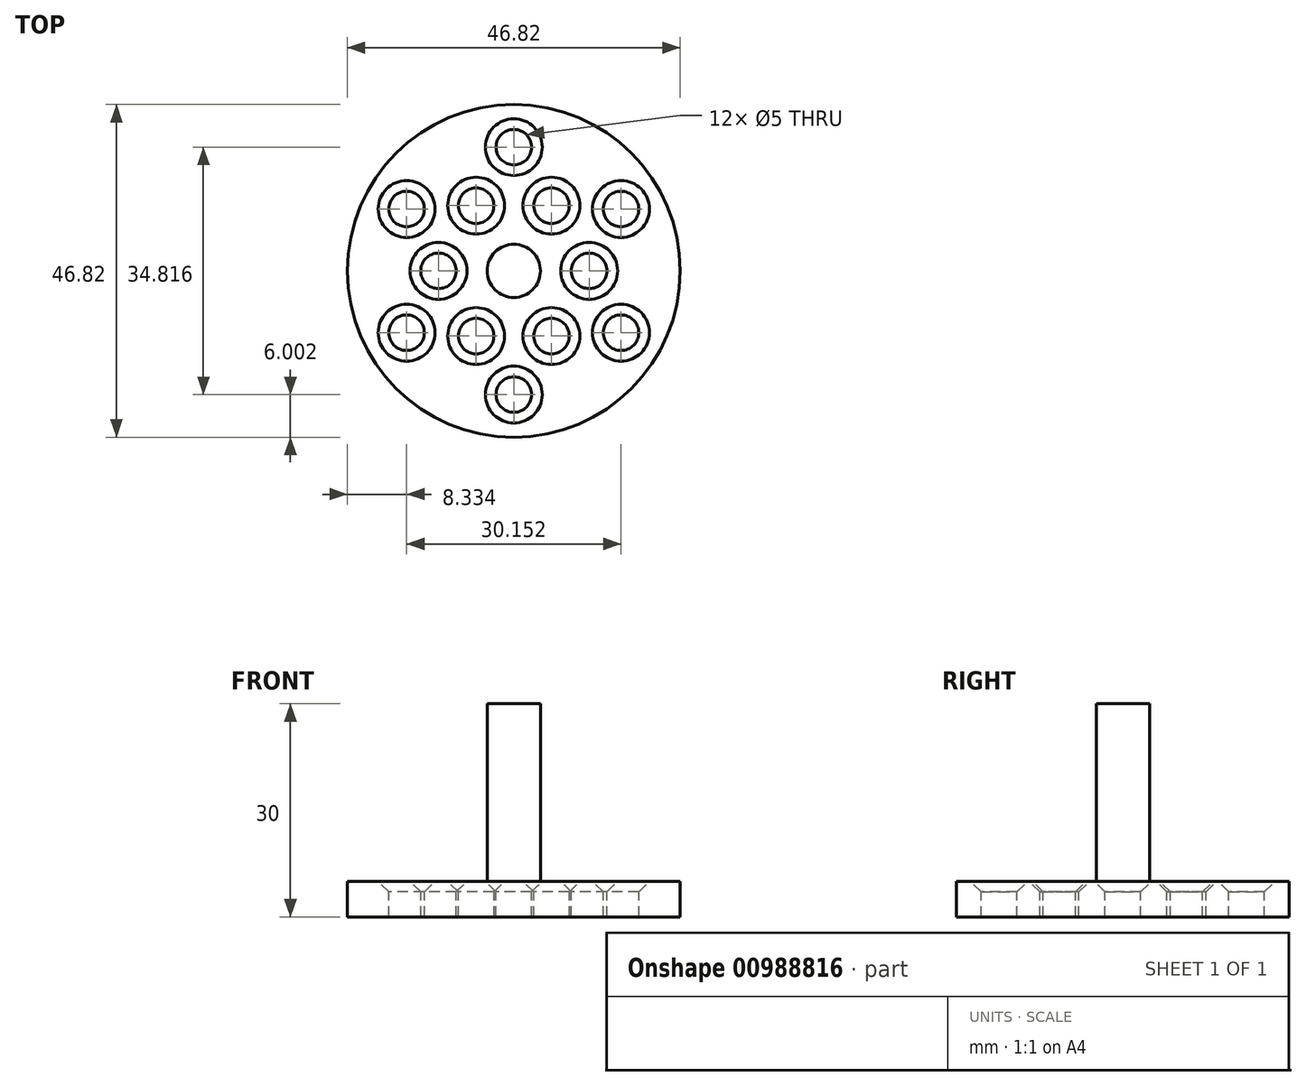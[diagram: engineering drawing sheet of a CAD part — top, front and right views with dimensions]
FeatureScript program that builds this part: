
annotation { "Feature Type Name" : "Feature", "Feature Type Description" : "" }
export const myFeature = defineFeature(function(context is Context, id is Id, definition is map)
    precondition{}
    {
        {
            var Q0;
            Q0=qCreatedBy(makeId("Top.planeOp"),FACE);
            var sketch = newSketch(context, id + "F0", { "sketchPlane" : qUnion([Q0])});
            skLineSegment(sketch, "E0.bottom", {"start": v(-25, 25) * mm, "end": v(25, 25) * mm});
            skLineSegment(sketch, "E0.top", {"start": v(-25, -25) * mm, "end": v(25, -25) * mm});
            skLineSegment(sketch, "E0.left", {"start": v(-25, 25) * mm, "end": v(-25, -25) * mm});
            skLineSegment(sketch, "E0.right", {"start": v(25, 25) * mm, "end": v(25, -25) * mm});
            skPoint(sketch, "E0.middle", {"position": v(0, 0) * mm});
            skSolve(sketch);
        }
        {
            var Q0;
            Q0=qSketchRegion(id+"F0",true);
            extrude(context, id + "F1", {"entities" : qUnion([Q0]), "depth" : 5 * mm, "offsetDistance" : 25 * mm});
        }
        {
            var Q0;
            Q0=makeQuery(id+"F1.opExtrude","CAP_FACE",FACE,{"disambiguationData":[OSD([sQuery(id+"F0.wireOp",EDGE,"E0.bottom"),sQuery(id+"F0.wireOp",EDGE,"E0.top"),sQuery(id+"F0.wireOp",EDGE,"E0.left"),sQuery(id+"F0.wireOp",EDGE,"E0.right")])],"isStart":false});
            var sketch = newSketch(context, id + "F2", { "sketchPlane" : qUnion([Q0])});
            skCircle(sketch, "E1.cCircle", {"center": v(0, 0) * mm, "radius": 15.08 * mm, "construction": true});
            skLineSegment(sketch, "E1.0", {"start": v(-15.08, -8.7) * mm, "end": v(-15.08, 8.7) * mm});
            skLineSegment(sketch, "E1.1", {"start": v(-15.08, 8.7) * mm, "end": v(0, 17.4) * mm});
            skLineSegment(sketch, "E1.2", {"start": v(0, 17.4) * mm, "end": v(15.08, 8.7) * mm});
            skLineSegment(sketch, "E1.3", {"start": v(15.08, 8.7) * mm, "end": v(15.08, -8.7) * mm});
            skLineSegment(sketch, "E1.4", {"start": v(15.08, -8.7) * mm, "end": v(0, -17.4) * mm});
            skLineSegment(sketch, "E1.5", {"start": v(0, -17.4) * mm, "end": v(-15.08, -8.7) * mm});
            skPoint(sketch, "E1.0.midPoint", {"position": v(-15.08, 0) * mm});
            skSolve(sketch);
        }
        {
            var Q0;
            Q0=sQuery(id+"F2.wireOp",VERTEX,"E1.1.end");
            var Q1;
            Q1=sQuery(id+"F2.wireOp",VERTEX,"E1.2.end");
            var Q2;
            Q2=sQuery(id+"F2.wireOp",VERTEX,"E1.3.end");
            var Q3;
            Q3=sQuery(id+"F2.wireOp",VERTEX,"E1.4.end");
            var Q4;
            Q4=sQuery(id+"F2.wireOp",VERTEX,"E1.0.start");
            var Q5;
            Q5=sQuery(id+"F2.wireOp",VERTEX,"E1.0.end");
            var Q6;
            Q6=makeQuery(id+"F1.opExtrude","SWEPT_BODY",BODY,{"disambiguationData":[OSD([sQuery(id+"F0.wireOp",EDGE,"E0.bottom"),sQuery(id+"F0.wireOp",EDGE,"E0.top"),sQuery(id+"F0.wireOp",EDGE,"E0.left"),sQuery(id+"F0.wireOp",EDGE,"E0.right")])]});
            hole(context, id + "F3", {"style" : HoleStyle.C_SINK, "endStyle" : HoleEndStyle.THROUGH, "holeDiameter" : 5 * mm, "cSinkDiameter" : 8 * mm, "cSinkAngle" : 90 * degree, "majorDiameter" : 5 * mm, "isTappedThrough" : true, "tappedDepth" : 12 * mm, "tapClearance" : 3, "locations" : qUnion([Q0, Q1, Q2, Q3, Q4, Q5]), "scope" : qUnion([Q6])});
        }
        {
            var Q0;
            Q0=makeQuery(id+"F1.opExtrude","CAP_FACE",FACE,{"disambiguationData":[OSD([sQuery(id+"F0.wireOp",EDGE,"E0.bottom"),sQuery(id+"F0.wireOp",EDGE,"E0.top"),sQuery(id+"F0.wireOp",EDGE,"E0.left"),sQuery(id+"F0.wireOp",EDGE,"E0.right")])],"isStart":false});
            var sketch = newSketch(context, id + "F4", { "sketchPlane" : qUnion([Q0])});
            skCircle(sketch, "E2", {"center": v(0, 0) * mm, "radius": 23.4 * mm});
            skSolve(sketch);
        }
        {
            var Q0;
            Q0 = qSketchRegion(id + "F4", true);
            extrude(context, id + "F5", {"entities" : qUnion([Q0]), "operationType" : NewBodyOperationType.INTERSECT, "oppositeDirection" : true, "depth" : 25 * mm, "offsetDistance" : 25 * mm});
        }
        {
            var Q0;
            Q0=makeQuery(id+"F1.opExtrude","CAP_FACE",FACE,{"disambiguationData":[OSD([sQuery(id+"F0.wireOp",EDGE,"E0.bottom"),sQuery(id+"F0.wireOp",EDGE,"E0.top"),sQuery(id+"F0.wireOp",EDGE,"E0.left"),sQuery(id+"F0.wireOp",EDGE,"E0.right")])],"isStart":false});
            var sketch = newSketch(context, id + "F6", { "sketchPlane" : qUnion([Q0])});
            skCircle(sketch, "E3.cCircle", {"center": v(0, 0) * mm, "radius": 9.18 * mm, "construction": true});
            skLineSegment(sketch, "E3.0", {"start": v(5.3, -9.18) * mm, "end": v(-5.3, -9.18) * mm});
            skLineSegment(sketch, "E3.1", {"start": v(-5.3, -9.18) * mm, "end": v(-10.6, 0) * mm});
            skLineSegment(sketch, "E3.2", {"start": v(-10.6, 0) * mm, "end": v(-5.3, 9.18) * mm});
            skLineSegment(sketch, "E3.3", {"start": v(-5.3, 9.18) * mm, "end": v(5.3, 9.18) * mm});
            skLineSegment(sketch, "E3.4", {"start": v(5.3, 9.18) * mm, "end": v(10.6, 0) * mm});
            skLineSegment(sketch, "E3.5", {"start": v(10.6, 0) * mm, "end": v(5.3, -9.18) * mm});
            skPoint(sketch, "E3.0.midPoint", {"position": v(0, -9.18) * mm});
            skSolve(sketch);
        }
        {
            var Q0;
            Q0=sQuery(id+"F6.wireOp",VERTEX,"E3.2.end");
            var Q1;
            Q1=sQuery(id+"F6.wireOp",VERTEX,"E3.3.end");
            var Q2;
            Q2=sQuery(id+"F6.wireOp",VERTEX,"E3.4.end");
            var Q3;
            Q3=sQuery(id+"F6.wireOp",VERTEX,"E3.0.start");
            var Q4;
            Q4=sQuery(id+"F6.wireOp",VERTEX,"E3.0.end");
            var Q5;
            Q5=sQuery(id+"F6.wireOp",VERTEX,"E3.1.end");
            var Q6;
            Q6=makeQuery(id+"F1.opExtrude","SWEPT_BODY",BODY,{"disambiguationData":[OSD([sQuery(id+"F0.wireOp",EDGE,"E0.bottom"),sQuery(id+"F0.wireOp",EDGE,"E0.top"),sQuery(id+"F0.wireOp",EDGE,"E0.left"),sQuery(id+"F0.wireOp",EDGE,"E0.right")])]});
            hole(context, id + "F7", {"style" : HoleStyle.C_SINK, "endStyle" : HoleEndStyle.THROUGH, "holeDiameter" : 5 * mm, "cSinkDiameter" : 8 * mm, "cSinkAngle" : 90 * degree, "majorDiameter" : 5 * mm, "isTappedThrough" : true, "tappedDepth" : 12 * mm, "tapClearance" : 3, "locations" : qUnion([Q0, Q1, Q2, Q3, Q4, Q5]), "scope" : qUnion([Q6])});
        }
        {
            var Q0;
            Q0=makeQuery(id+"F1.opExtrude","CAP_FACE",FACE,{"disambiguationData":[OSD([sQuery(id+"F0.wireOp",EDGE,"E0.bottom"),sQuery(id+"F0.wireOp",EDGE,"E0.top"),sQuery(id+"F0.wireOp",EDGE,"E0.left"),sQuery(id+"F0.wireOp",EDGE,"E0.right")])],"isStart":false});
            var sketch = newSketch(context, id + "F8", { "sketchPlane" : qUnion([Q0])});
            skCircle(sketch, "E4", {"center": v(0, 0) * mm, "radius": 3.74 * mm});
            skSolve(sketch);
        }
        {
            var Q0;
            Q0=makeQuery(id+"F8.imprint","IMPRINT",FACE,{"disambiguationData":[TD([[makeQuery(id+"F8.imprint","IMPRINT",EDGE,{"derivedFrom":sQuery(id+"F8.wireOp",EDGE,"E4")}),1.0]])]});
            extrude(context, id + "F9", {"entities" : qUnion([Q0]), "operationType" : NewBodyOperationType.ADD, "depth" : 25 * mm, "offsetDistance" : 25 * mm});
        }
    });
